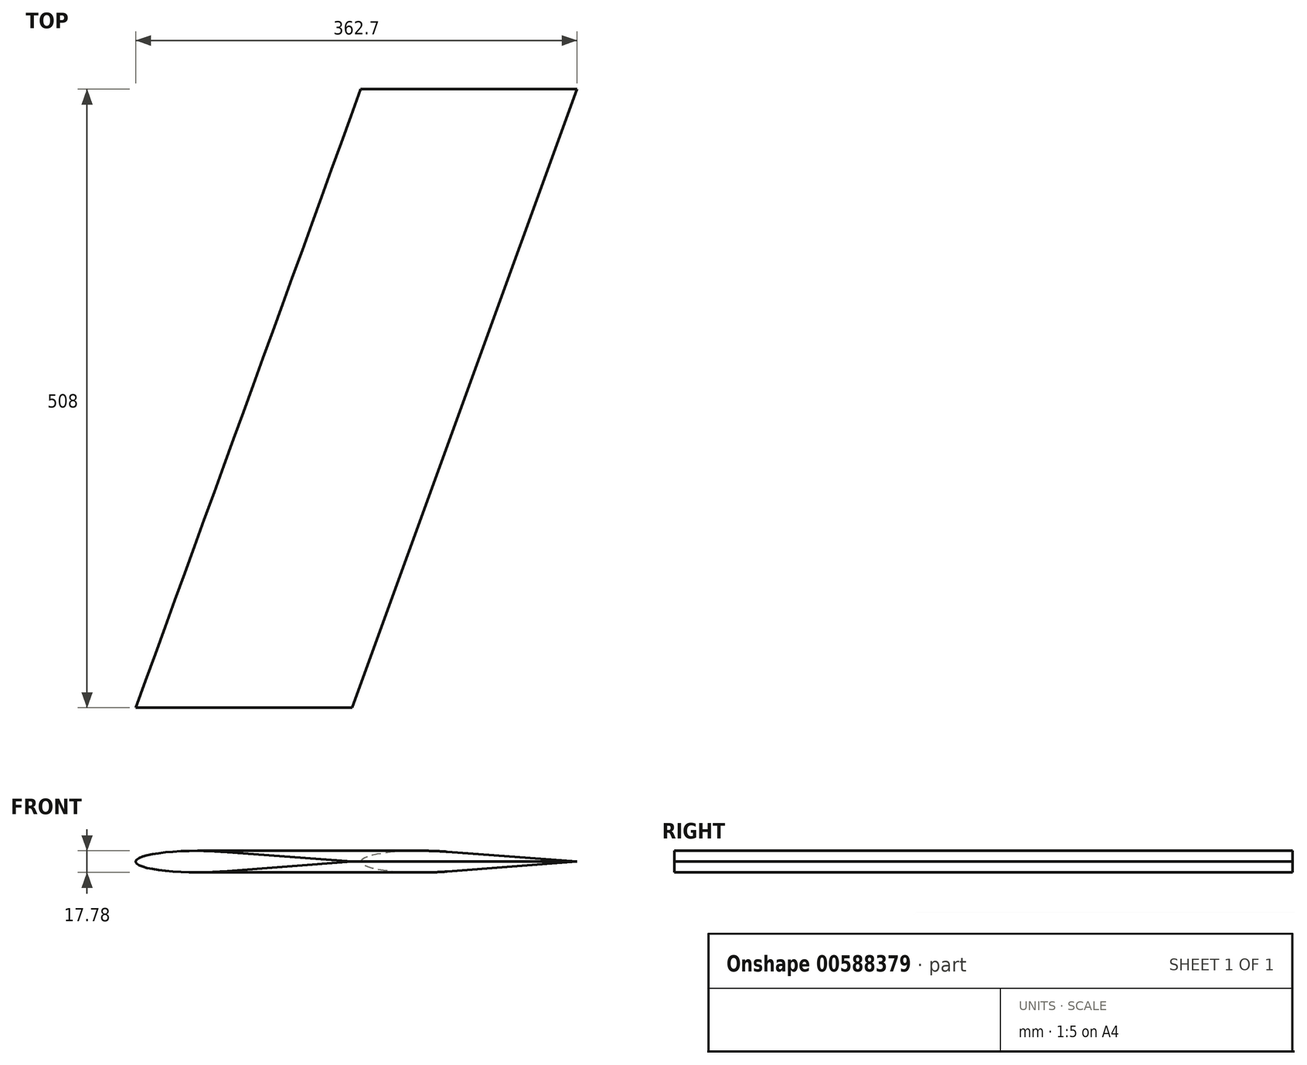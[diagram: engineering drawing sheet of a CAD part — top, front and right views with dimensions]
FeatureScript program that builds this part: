
annotation { "Feature Type Name" : "Feature", "Feature Type Description" : "" }
export const myFeature = defineFeature(function(context is Context, id is Id, definition is map)
    precondition{}
    {
        {
            var Q0;
            Q0=qCreatedBy(makeId("Front.planeOp"),FACE);
            var sketch = newSketch(context, id + "F0", { "sketchPlane" : qUnion([Q0])});
            skEllipse(sketch, "E0", {"center": v(50.8, 0) * mm, "majorRadius": 50.8 * mm, "minorRadius": 8.9 * mm, "majorAxis": v(-1, 0)});
            skLineSegment(sketch, "E1", {"start": v(71.12, 8.15) * mm, "end": v(177.8, 0) * mm});
            skLineSegment(sketch, "E2", {"start": v(177.8, 0) * mm, "end": v(71.12, -8.15) * mm});
            skLineSegment(sketch, "E3", {"start": v(177.8, 0) * mm, "end": v(0, 0) * mm, "construction": true});
            skSolve(sketch);
        }
        {
            var Q0;
            Q0=qCreatedBy(makeId("Top.planeOp"),FACE);
            var sketch = newSketch(context, id + "F1", { "sketchPlane" : qUnion([Q0])});
            skLineSegment(sketch, "E4", {"start": v(0, 0) * mm, "end": v(184.9, 508) * mm});
            skSolve(sketch);
        }
        {
            var Q0;
            Q0 = qSketchRegion(id + "F0", true);
            var Q1;
            Q1 = qConstructionFilter(qBodyType(qCreatedBy(id + "F1" ,EDGE), BodyType.WIRE), ConstructionObject.NO);
            sweep(context, id + "F2", {"profiles" : qUnion([Q0]), "path" : qUnion([Q1])});
        }
    });
